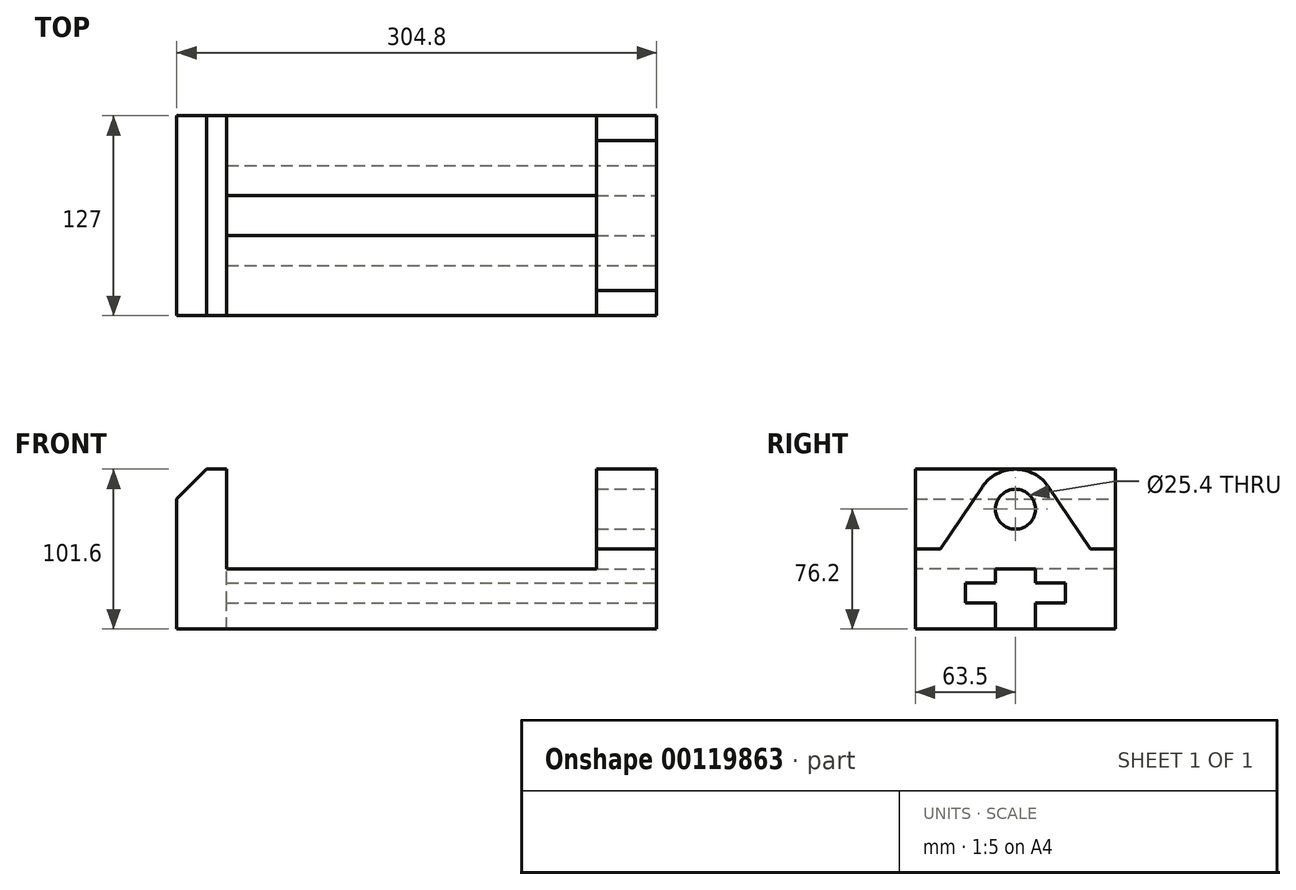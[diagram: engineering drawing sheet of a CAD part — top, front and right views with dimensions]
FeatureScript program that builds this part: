
annotation { "Feature Type Name" : "Feature", "Feature Type Description" : "" }
export const myFeature = defineFeature(function(context is Context, id is Id, definition is map)
    precondition{}
    {
        {
            var Q0;
            Q0=qCreatedBy(makeId("Front.planeOp"),FACE);
            var sketch = newSketch(context, id + "F0", { "sketchPlane" : qUnion([Q0])});
            skLineSegment(sketch, "E0", {"start": v(0, 0) * mm, "end": v(304.8, 0) * mm});
            skLineSegment(sketch, "E1", {"start": v(304.8, 0) * mm, "end": v(304.8, 101.6) * mm});
            skLineSegment(sketch, "E2", {"start": v(304.8, 101.6) * mm, "end": v(266.7, 101.6) * mm});
            skLineSegment(sketch, "E3", {"start": v(266.7, 101.6) * mm, "end": v(266.7, 38.1) * mm});
            skLineSegment(sketch, "E4", {"start": v(266.7, 38.1) * mm, "end": v(31.75, 38.1) * mm});
            skLineSegment(sketch, "E5", {"start": v(31.75, 38.1) * mm, "end": v(31.75, 101.6) * mm});
            skLineSegment(sketch, "E6", {"start": v(31.75, 101.6) * mm, "end": v(0, 101.6) * mm});
            skLineSegment(sketch, "E7", {"start": v(0, 101.6) * mm, "end": v(0, 0) * mm});
            skSolve(sketch);
        }
        {
            var Q0;
            Q0 = qSketchRegion(id + "F0", true);
            extrude(context, id + "F1", {"entities" : qUnion([Q0]), "oppositeDirection" : true, "depth" : 127 * mm});
        }
        {
            var Q0;
            Q0=makeQuery(id+"F1.opExtrude","SWEPT_EDGE",EDGE,{"disambiguationData":[OSD([sQuery(id+"F0.wireOp",EDGE,"E6"),sQuery(id+"F0.wireOp",EDGE,"E7")])]});
            chamfer(context, id + "F2", {"entities" : qUnion([Q0]), "chamferType" : ChamferType.TWO_OFFSETS, "width1" : 19.05 * mm, "oppositeDirection" : false, "width2" : 19.05 * mm, "tangentPropagation" : true});
        }
        {
            var Q0;
            Q0=makeQuery(id+"F1.opExtrude","SWEPT_FACE",FACE,{"disambiguationData":[OSD([sQuery(id+"F0.wireOp",EDGE,"E1")])]});
            var sketch = newSketch(context, id + "F3", { "sketchPlane" : qUnion([Q0])});
            skLineSegment(sketch, "E8", {"start": v(0, 50.8) * mm, "end": v(15.87, 50.8) * mm});
            skLineSegment(sketch, "E9", {"start": v(15.87, 50.8) * mm, "end": v(42.4, 90.35) * mm});
            skLineSegment(sketch, "E10", {"start": v(127, 50.8) * mm, "end": v(111.12, 50.8) * mm});
            skLineSegment(sketch, "E11", {"start": v(111.13, 50.8) * mm, "end": v(84.6, 90.35) * mm});
            skArc(sketch, "E12", {"start": v(84.6, 90.35) * mm, "mid": v(63.5, 101.6) * mm, "end": v(42.4, 90.35) * mm});
            skSolve(sketch);
        }
        {
            var Q0;
            {var subQ7=sQuery(id+"F3.wireOp",EDGE,"E8");Q0=makeQuery(id+"F3.imprint","IMPRINT",FACE,{"disambiguationData":[TD([[makeQuery(id+"F3.imprint","IMPRINT",EDGE,{"derivedFrom":subQ7}),1.0]])]});}
            var Q1;
            {var subQ7=sQuery(id+"F3.wireOp",EDGE,"E10");Q1=makeQuery(id+"F3.imprint","IMPRINT",FACE,{"disambiguationData":[TD([[makeQuery(id+"F3.imprint","IMPRINT",EDGE,{"derivedFrom":subQ7}),-1.0]])]});}
            extrude(context, id + "F4", {"entities" : qUnion([Q0, Q1]), "operationType" : NewBodyOperationType.REMOVE, "oppositeDirection" : true, "depth" : 38.1 * mm});
        }
        {
            var Q0;
            Q0=makeQuery(id+"F1.opExtrude","SWEPT_FACE",FACE,{"disambiguationData":[OSD([sQuery(id+"F0.wireOp",EDGE,"E1")])]});
            var sketch = newSketch(context, id + "F5", { "sketchPlane" : qUnion([Q0])});
            skCircle(sketch, "E13", {"center": v(63.5, 76.2) * mm, "radius": 12.7 * mm});
            skSolve(sketch);
        }
        {
            var Q0;
            Q0 = qSketchRegion(id + "F5", true);
            extrude(context, id + "F6", {"entities" : qUnion([Q0]), "operationType" : NewBodyOperationType.REMOVE, "oppositeDirection" : true, "depth" : 38.1 * mm});
        }
        {
            var Q0;
            {var subQ6=sQuery(id+"F3.wireOp",EDGE,"E8");Q0=makeQuery(id+"F3.imprint","IMPRINT",FACE,{"disambiguationData":[TD([[makeQuery(id+"F3.imprint","IMPRINT",EDGE,{"derivedFrom":subQ6}),-1.0]])]});}
            var sketch = newSketch(context, id + "F7", { "sketchPlane" : qUnion([Q0])});
            skLineSegment(sketch, "E14", {"start": v(50.8, 0) * mm, "end": v(50.8, 16.5) * mm});
            skLineSegment(sketch, "E15", {"start": v(50.8, 16.5) * mm, "end": v(31.75, 16.5) * mm});
            skLineSegment(sketch, "E16", {"start": v(31.75, 16.5) * mm, "end": v(31.75, 29.2) * mm});
            skLineSegment(sketch, "E17", {"start": v(31.75, 29.2) * mm, "end": v(50.8, 29.21) * mm});
            skLineSegment(sketch, "E18", {"start": v(50.8, 29.21) * mm, "end": v(50.8, 38.1) * mm});
            skLineSegment(sketch, "E19", {"start": v(50.8, 38.1) * mm, "end": v(76.2, 38.1) * mm});
            skLineSegment(sketch, "E20", {"start": v(76.2, 38.1) * mm, "end": v(76.2, 29.21) * mm});
            skLineSegment(sketch, "E21", {"start": v(76.2, 29.21) * mm, "end": v(95.25, 29.21) * mm});
            skLineSegment(sketch, "E22", {"start": v(95.25, 29.21) * mm, "end": v(95.25, 16.51) * mm});
            skLineSegment(sketch, "E23", {"start": v(95.25, 16.5) * mm, "end": v(76.2, 16.5) * mm});
            skLineSegment(sketch, "E24", {"start": v(76.2, 16.5) * mm, "end": v(76.2, 0) * mm});
            skLineSegment(sketch, "E25", {"start": v(50.8, 0) * mm, "end": v(76.2, 0) * mm});
            skSolve(sketch);
        }
        {
            var Q0;
            Q0 = qSketchRegion(id + "F7", true);
            extrude(context, id + "F8", {"entities" : qUnion([Q0]), "operationType" : NewBodyOperationType.REMOVE, "oppositeDirection" : true, "depth" : 273.05 * mm});
        }
    });
